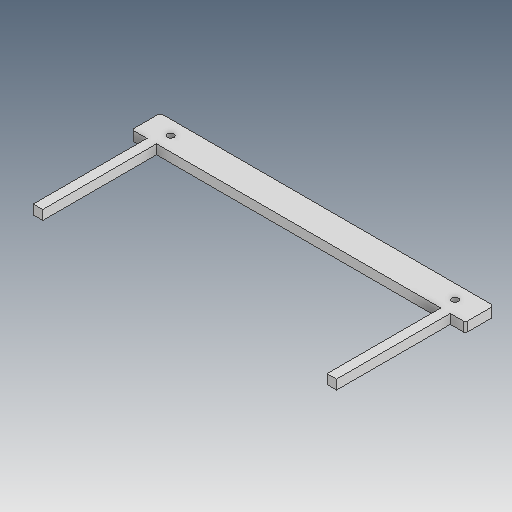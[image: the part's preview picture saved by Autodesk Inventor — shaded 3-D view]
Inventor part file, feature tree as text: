
AUTODESK INVENTOR PART (.ipt)
format: ipt  version: 2020 (Build 240168000, 168)  size: 114,688 bytes
history: native  units: mm
features: other x3, sketch x3
ambient origin geometry x8: Origin, YZ Plane, XZ Plane, XY Plane, X Axis, Y Axis, Z Axis, Center Point
bodies: Volumenkörper1 (feature_tree)
feature tree (6):
  other  "Gestell_Seite.ipt"
  other  "Volumenkörper1::Gestell_Seite.ipt"
  other  "Bezeichnung1"
  sketch  "Skizze1"  dims[d0=10.0mm]
  sketch  "Skizze2"
  sketch  "Skizze3"
